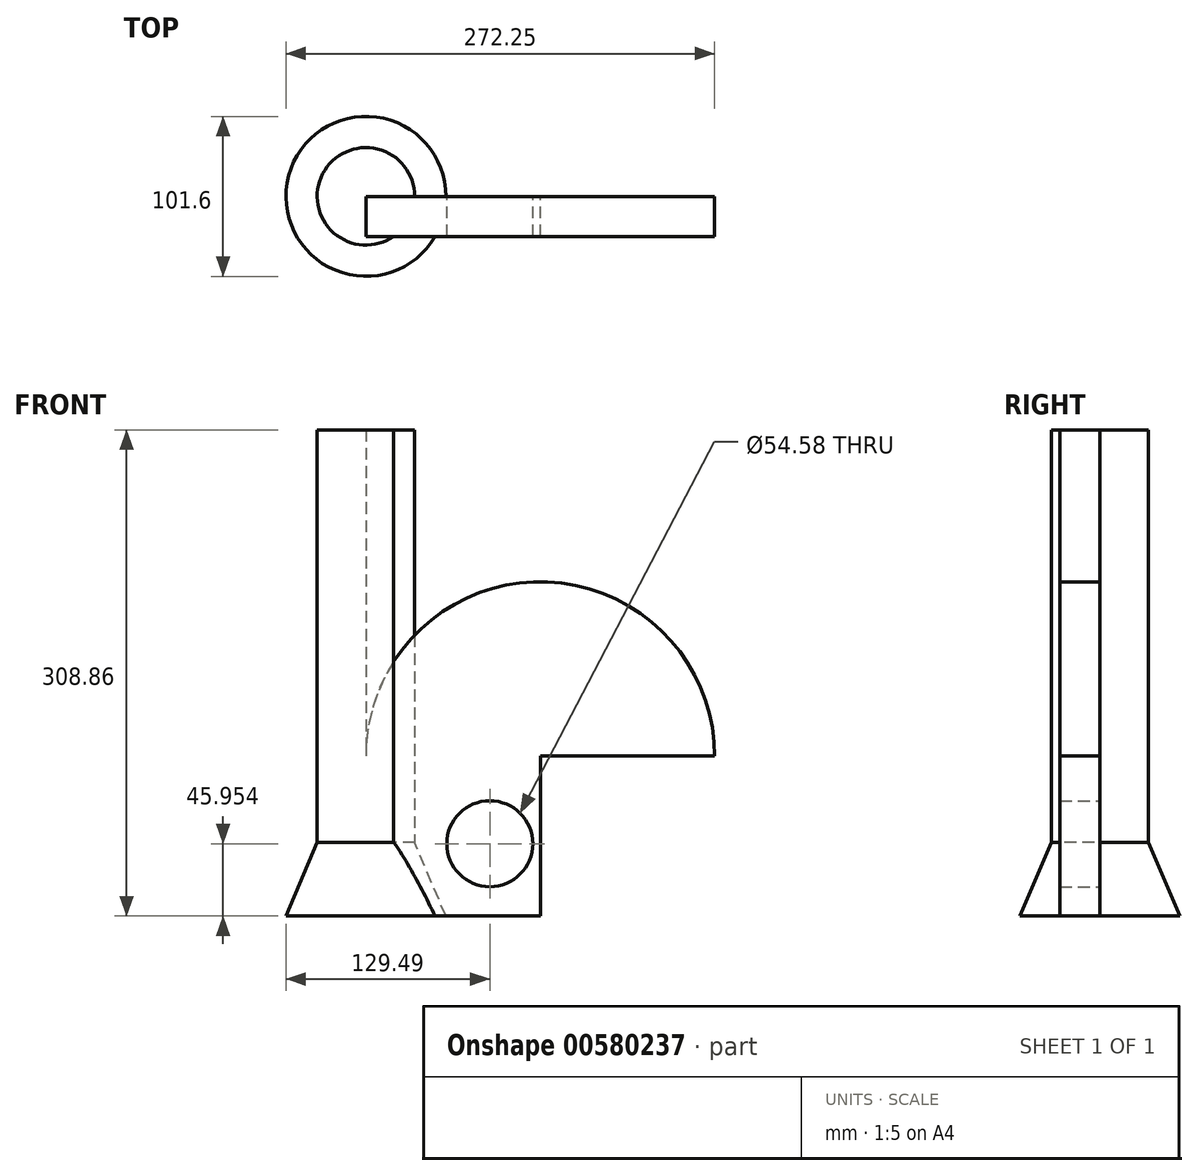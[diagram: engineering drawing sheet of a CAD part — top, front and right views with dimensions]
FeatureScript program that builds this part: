
annotation { "Feature Type Name" : "Feature", "Feature Type Description" : "" }
export const myFeature = defineFeature(function(context is Context, id is Id, definition is map)
    precondition{}
    {
        {
            var Q0;
            Q0=qCreatedBy(makeId("Front.planeOp"),FACE);
            var sketch = newSketch(context, id + "F0", { "sketchPlane" : qUnion([Q0])});
            skLineSegment(sketch, "E0.bottom", {"start": v(0, 0) * mm, "end": v(110.73, 0) * mm});
            skLineSegment(sketch, "E0.top", {"start": v(0, 101.6) * mm, "end": v(110.73, 101.6) * mm});
            skLineSegment(sketch, "E0.left", {"start": v(0, 0) * mm, "end": v(0, 101.6) * mm});
            skLineSegment(sketch, "E0.right", {"start": v(110.73, 0) * mm, "end": v(110.73, 101.6) * mm});
            skCircle(sketch, "E1", {"center": v(78.69, 45.95) * mm, "radius": 27.29 * mm});
            skSolve(sketch);
        }
        {
            var Q0;
            Q0 = qSketchRegion(id + "F0", true);
            extrude(context, id + "F1", {"entities" : qUnion([Q0]), "depth" : 25.4 * mm, "offsetDistance" : 25.4 * mm});
        }
        {
            var Q0;
            Q0=qCreatedBy(makeId("Front.planeOp"),FACE);
            var sketch = newSketch(context, id + "F2", { "sketchPlane" : qUnion([Q0])});
            skLineSegment(sketch, "E2", {"start": v(0, 0) * mm, "end": v(-50.8, 0) * mm});
            skLineSegment(sketch, "E3", {"start": v(-50.8, 0) * mm, "end": v(-30.93, 46.75) * mm});
            skLineSegment(sketch, "E4", {"start": v(-31.2, 46.73) * mm, "end": v(0, 46.73) * mm});
            skLineSegment(sketch, "E5", {"start": v(0, 46.73) * mm, "end": v(0, 0) * mm});
            skLineSegment(sketch, "E6", {"start": v(0, 0) * mm, "end": v(-1727.68, -9137.88) * mm});
            skLineSegment(sketch, "E7", {"start": v(-1727.68, -9137.88) * mm, "end": v(75.14, 0) * mm});
            skLineSegment(sketch, "E8", {"start": v(75.14, 6.53) * mm, "end": v(0, 0) * mm});
            skSolve(sketch);
        }
        {
            var Q0;
            {var subQ0=sQuery(id+"F2.wireOp",EDGE,"E2");Q0=makeQuery(id+"F2.imprint","IMPRINT",FACE,{"disambiguationData":[TD([[makeQuery(id+"F2.imprint","IMPRINT",EDGE,{"derivedFrom":subQ0}),-1.0]])]});}
            var Q1;
            Q1=sQuery(id+"F2.wireOp",EDGE,"E5");
            revolve(context, id + "F3", {"operationType" : NewBodyOperationType.ADD, "entities" : qUnion([Q0]), "axis" : qUnion([Q1]), "revolveType" : RevolveType.FULL});
        }
        {
            var Q0;
            Q0=makeQuery(id+"F3.opRevolve","SWEPT_FACE",FACE,{"disambiguationData":[OSD([sQuery(id+"F2.wireOp",EDGE,"E4")])]});
            extrude(context, id + "F4", {"entities" : qUnion([Q0]), "operationType" : NewBodyOperationType.ADD, "depth" : 262.13 * mm, "offsetDistance" : 25.4 * mm});
        }
        {
            var Q0;
            Q0=makeQuery(id+"F1.opExtrude","SWEPT_FACE",FACE,{"disambiguationData":[OSD([sQuery(id+"F0.wireOp",EDGE,"E0.top")])]});
            var Q1;
            Q1=makeQuery(id+"F1.opExtrude","SWEPT_EDGE",EDGE,{"disambiguationData":[OSD([sQuery(id+"F0.wireOp",EDGE,"E0.top"),sQuery(id+"F0.wireOp",EDGE,"E0.right")])]});
            revolve(context, id + "F5", {"operationType" : NewBodyOperationType.ADD, "entities" : qUnion([Q0]), "axis" : qUnion([Q1]), "revolveType" : RevolveType.ONE_DIRECTION, "angle" : 180 * degree});
        }
    });
